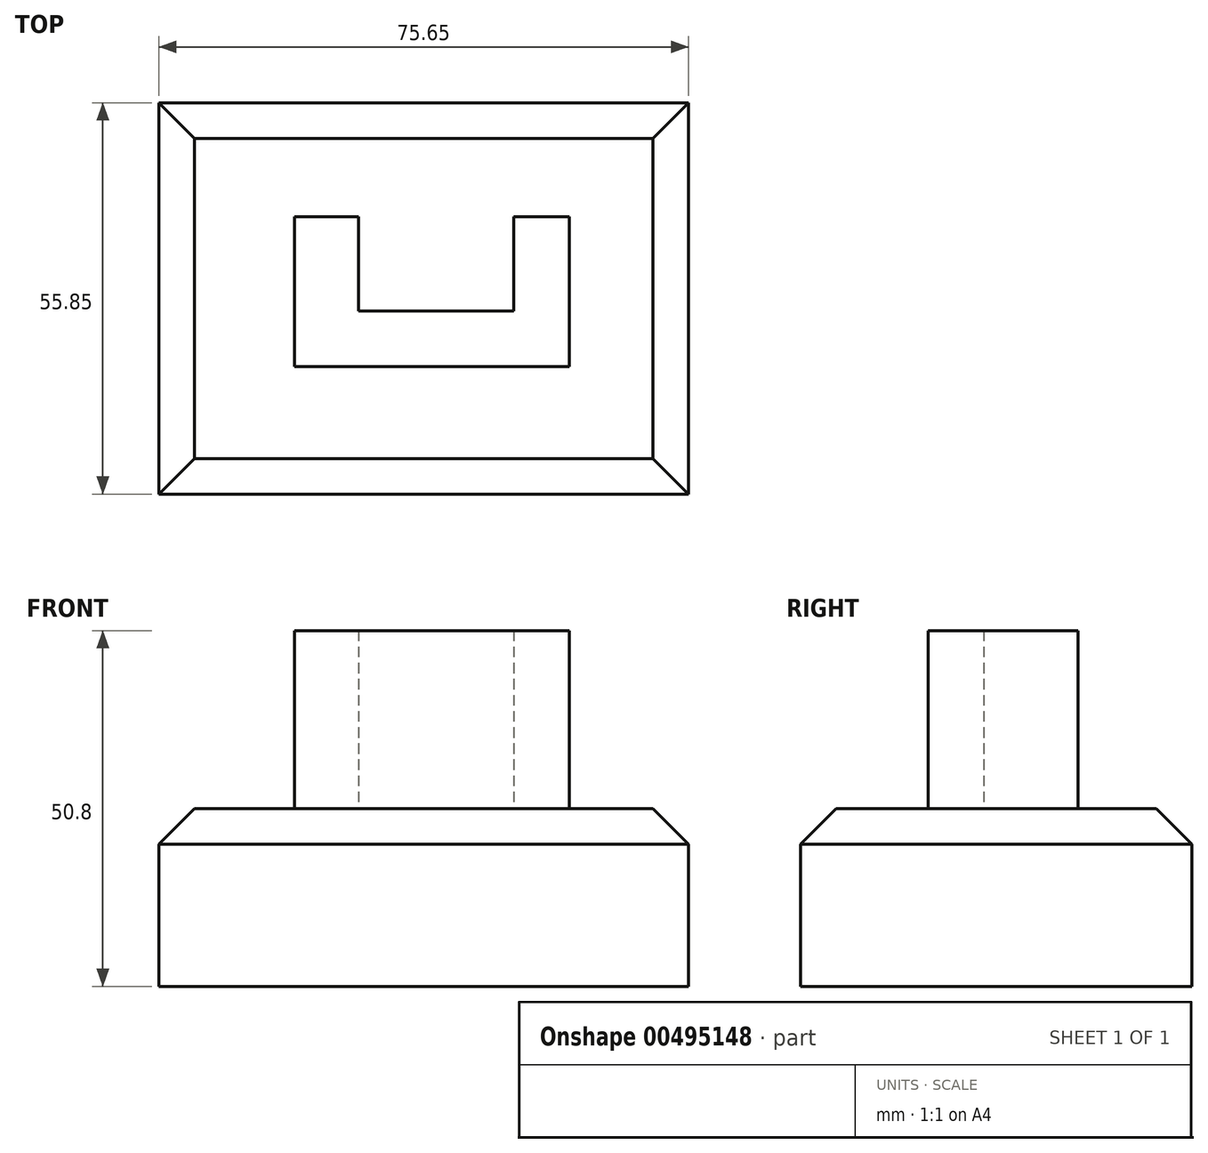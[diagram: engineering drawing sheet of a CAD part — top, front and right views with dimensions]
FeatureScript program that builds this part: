
annotation { "Feature Type Name" : "Feature", "Feature Type Description" : "" }
export const myFeature = defineFeature(function(context is Context, id is Id, definition is map)
    precondition{}
    {
        {
            var Q0;
            Q0=qCreatedBy(makeId("Top.planeOp"),FACE);
            var sketch = newSketch(context, id + "F0", { "sketchPlane" : qUnion([Q0])});
            skLineSegment(sketch, "E0.bottom", {"start": v(0, 0) * mm, "end": v(75.65, 0) * mm});
            skLineSegment(sketch, "E0.top", {"start": v(0, 55.85) * mm, "end": v(75.65, 55.85) * mm});
            skLineSegment(sketch, "E0.left", {"start": v(0, 0) * mm, "end": v(0, 55.85) * mm});
            skLineSegment(sketch, "E0.right", {"start": v(75.65, 0) * mm, "end": v(75.65, 55.85) * mm});
            skSolve(sketch);
        }
        {
            var Q0;
            Q0 = qSketchRegion(id + "F0", true);
            extrude(context, id + "F1", {"entities" : qUnion([Q0]), "oppositeDirection" : true, "depth" : 25.4 * mm});
        }
        {
            var Q0;
            Q0=makeQuery(id+"F1.opExtrude","CAP_EDGE",EDGE,{"disambiguationData":[OSD([sQuery(id+"F0.wireOp",EDGE,"E0.left")])],"isStart":true});
            var Q1;
            Q1=makeQuery(id+"F1.opExtrude","CAP_FACE",FACE,{"disambiguationData":[OSD([sQuery(id+"F0.wireOp",EDGE,"E0.bottom"),sQuery(id+"F0.wireOp",EDGE,"E0.top"),sQuery(id+"F0.wireOp",EDGE,"E0.left"),sQuery(id+"F0.wireOp",EDGE,"E0.right")])],"isStart":true});
            chamfer(context, id + "F2", {"entities" : qUnion([Q0, Q1]), "width" : 5.08 * mm, "tangentPropagation" : true});
        }
        {
            var Q0;
            Q0=qCreatedBy(makeId("Top.planeOp"),FACE);
            var sketch = newSketch(context, id + "F3", { "sketchPlane" : qUnion([Q0])});
            skLineSegment(sketch, "E1", {"start": v(58.62, 39.6) * mm, "end": v(50.7, 39.6) * mm});
            skLineSegment(sketch, "E2", {"start": v(50.7, 39.6) * mm, "end": v(58.62, 39.6) * mm});
            skLineSegment(sketch, "E3", {"start": v(58.62, 18.22) * mm, "end": v(58.62, 39.6) * mm});
            skLineSegment(sketch, "E4", {"start": v(58.62, 18.22) * mm, "end": v(19.4, 18.22) * mm});
            skLineSegment(sketch, "E5", {"start": v(19.4, 18.22) * mm, "end": v(19.4, 39.6) * mm});
            skLineSegment(sketch, "E6", {"start": v(19.4, 39.6) * mm, "end": v(28.52, 39.6) * mm});
            skLineSegment(sketch, "E7", {"start": v(28.52, 39.6) * mm, "end": v(28.52, 26.14) * mm});
            skLineSegment(sketch, "E8", {"start": v(28.52, 26.14) * mm, "end": v(50.7, 26.14) * mm});
            skLineSegment(sketch, "E9", {"start": v(50.7, 26.14) * mm, "end": v(50.7, 39.6) * mm});
            skSolve(sketch);
        }
        {
            var Q0;
            Q0 = qSketchRegion(id + "F3", true);
            extrude(context, id + "F4", {"entities" : qUnion([Q0]), "operationType" : NewBodyOperationType.ADD, "depth" : 25.4 * mm});
        }
    });
